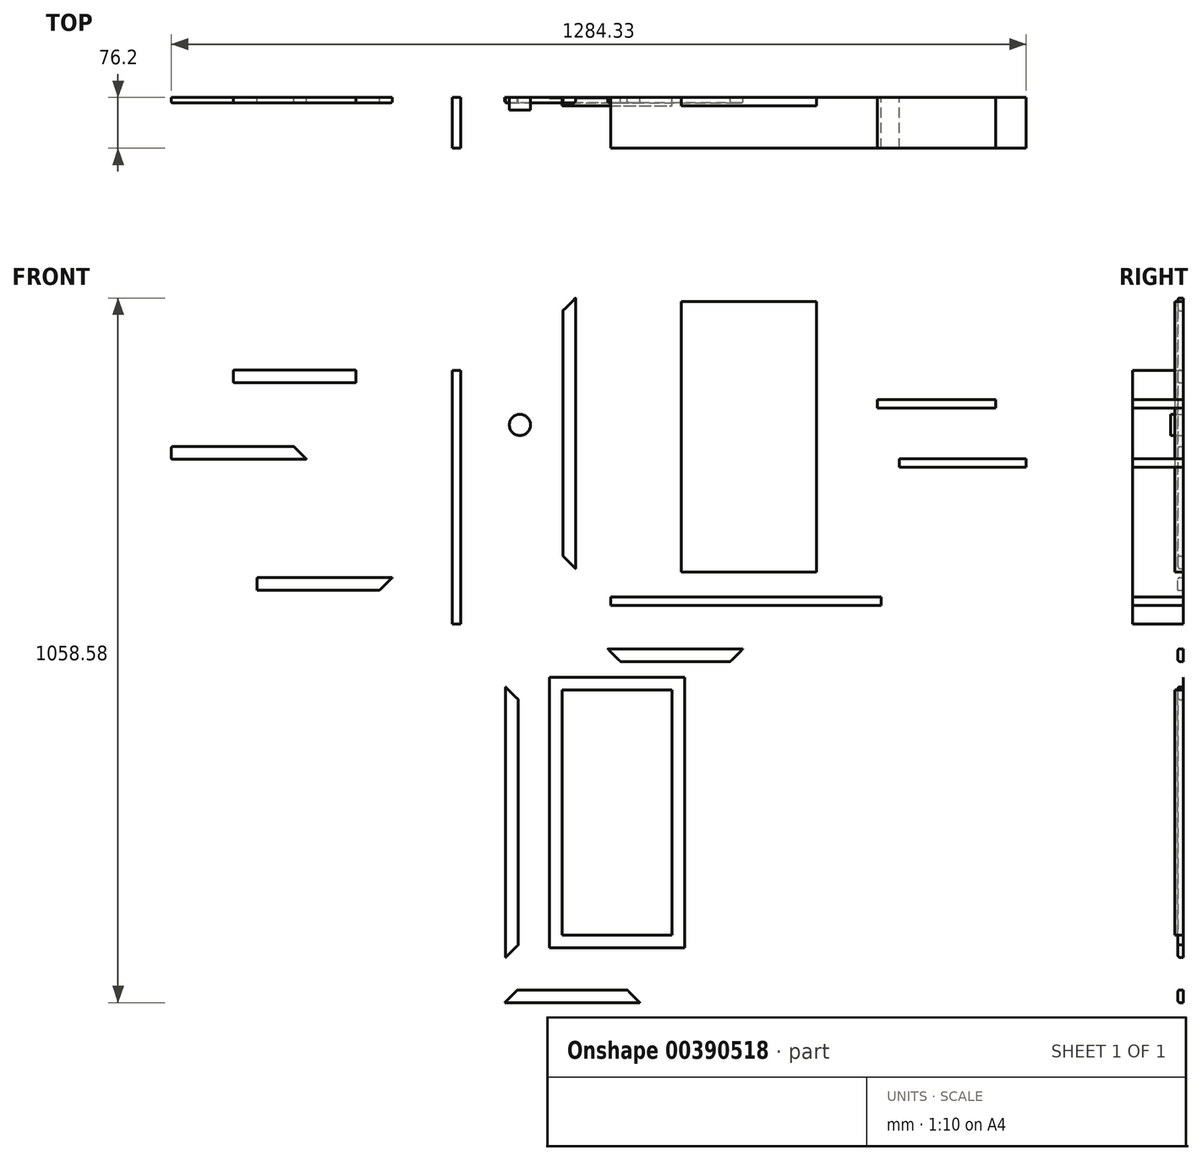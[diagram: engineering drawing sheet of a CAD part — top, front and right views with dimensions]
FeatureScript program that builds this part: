
annotation { "Feature Type Name" : "Feature", "Feature Type Description" : "" }
export const myFeature = defineFeature(function(context is Context, id is Id, definition is map)
    precondition{}
    {
        {
            var Q0;
            Q0=qCreatedBy(makeId("Front.planeOp"),FACE);
            var sketch = newSketch(context, id + "F0", { "sketchPlane" : qUnion([Q0])});
            skLineSegment(sketch, "E0.bottom", {"start": v(-101.6, 203.2) * mm, "end": v(101.6, 203.2) * mm});
            skLineSegment(sketch, "E0.top", {"start": v(-101.6, -203.2) * mm, "end": v(101.6, -203.2) * mm});
            skLineSegment(sketch, "E0.left", {"start": v(-101.6, 203.2) * mm, "end": v(-101.6, -203.2) * mm});
            skLineSegment(sketch, "E0.right", {"start": v(101.6, 203.2) * mm, "end": v(101.6, -203.2) * mm});
            skPoint(sketch, "E0.middle", {"position": v(0, 0) * mm});
            skSolve(sketch);
        }
        {
            var Q0;
            Q0 = qSketchRegion(id + "F0", true);
            extrude(context, id + "F1", {"entities" : qUnion([Q0]), "depth" : 12.7 * mm});
        }
        {
            var Q0;
            Q0=qCreatedBy(makeId("Front.planeOp"),FACE);
            var sketch = newSketch(context, id + "F2", { "sketchPlane" : qUnion([Q0])});
            skLineSegment(sketch, "E1.bottom", {"start": v(-445.4, 99.47) * mm, "end": v(-432.7, 99.47) * mm});
            skLineSegment(sketch, "E1.top", {"start": v(-445.4, -281.53) * mm, "end": v(-432.7, -281.53) * mm});
            skLineSegment(sketch, "E1.left", {"start": v(-445.4, 99.47) * mm, "end": v(-445.4, -281.53) * mm});
            skLineSegment(sketch, "E1.right", {"start": v(-432.7, 99.47) * mm, "end": v(-432.7, -281.53) * mm});
            skSolve(sketch);
        }
        {
            var Q0;
            Q0 = qSketchRegion(id + "F2", true);
            extrude(context, id + "F3", {"entities" : qUnion([Q0]), "depth" : 76.2 * mm});
        }
        {
            var Q0;
            Q0=qCreatedBy(makeId("Front.planeOp"),FACE);
            var sketch = newSketch(context, id + "F4", { "sketchPlane" : qUnion([Q0])});
            skLineSegment(sketch, "E2.bottom", {"start": v(-207.27, -253.72) * mm, "end": v(199.13, -253.72) * mm});
            skLineSegment(sketch, "E2.top", {"start": v(-207.27, -241.02) * mm, "end": v(199.13, -241.02) * mm});
            skLineSegment(sketch, "E2.left", {"start": v(-207.27, -253.72) * mm, "end": v(-207.27, -241.02) * mm});
            skLineSegment(sketch, "E2.right", {"start": v(199.13, -253.72) * mm, "end": v(199.13, -241.02) * mm});
            skSolve(sketch);
        }
        {
            var Q0;
            Q0 = qSketchRegion(id + "F4", true);
            extrude(context, id + "F5", {"entities" : qUnion([Q0]), "depth" : 76.2 * mm});
        }
        {
            var Q0;
            Q0=qCreatedBy(makeId("Front.planeOp"),FACE);
            var sketch = newSketch(context, id + "F6", { "sketchPlane" : qUnion([Q0])});
            skLineSegment(sketch, "E3.bottom", {"start": v(193.07, 55.39) * mm, "end": v(370.87, 55.39) * mm});
            skLineSegment(sketch, "E3.top", {"start": v(193.07, 42.69) * mm, "end": v(370.87, 42.69) * mm});
            skLineSegment(sketch, "E3.left", {"start": v(193.07, 55.39) * mm, "end": v(193.07, 42.69) * mm});
            skLineSegment(sketch, "E3.right", {"start": v(370.87, 55.39) * mm, "end": v(370.87, 42.69) * mm});
            skSolve(sketch);
        }
        {
            var Q0;
            Q0 = qSketchRegion(id + "F6", true);
            extrude(context, id + "F7", {"entities" : qUnion([Q0]), "depth" : 76.2 * mm});
        }
        {
            var Q0;
            Q0=qCreatedBy(makeId("Front.planeOp"),FACE);
            var sketch = newSketch(context, id + "F8", { "sketchPlane" : qUnion([Q0])});
            skLineSegment(sketch, "E4.bottom", {"start": v(226.2, -33.02) * mm, "end": v(416.7, -33.02) * mm});
            skLineSegment(sketch, "E4.top", {"start": v(226.2, -45.72) * mm, "end": v(416.7, -45.72) * mm});
            skLineSegment(sketch, "E4.left", {"start": v(226.2, -33.02) * mm, "end": v(226.2, -45.72) * mm});
            skLineSegment(sketch, "E4.right", {"start": v(416.7, -33.02) * mm, "end": v(416.7, -45.72) * mm});
            skSolve(sketch);
        }
        {
            var Q0;
            Q0 = qSketchRegion(id + "F8", true);
            extrude(context, id + "F9", {"entities" : qUnion([Q0]), "depth" : 76.2 * mm});
        }
        {
            var Q0;
            Q0=qCreatedBy(makeId("Front.planeOp"),FACE);
            var sketch = newSketch(context, id + "F10", { "sketchPlane" : qUnion([Q0])});
            skCircle(sketch, "E5", {"center": v(-343.97, 17.55) * mm, "radius": 15.88 * mm});
            skSolve(sketch);
        }
        {
            var Q0;
            Q0 = qSketchRegion(id + "F10", true);
            extrude(context, id + "F11", {"entities" : qUnion([Q0]), "depth" : 19.05 * mm});
        }
        {
            var Q0;
            Q0=qCreatedBy(makeId("Front.planeOp"),FACE);
            var sketch = newSketch(context, id + "F12", { "sketchPlane" : qUnion([Q0])});
            skLineSegment(sketch, "E6", {"start": v(-260.52, 208.27) * mm, "end": v(-279.57, 189.22) * mm});
            skLineSegment(sketch, "E7", {"start": v(-279.57, 189.22) * mm, "end": v(-279.57, -179.08) * mm});
            skLineSegment(sketch, "E8", {"start": v(-279.57, -179.08) * mm, "end": v(-260.52, -198.13) * mm});
            skLineSegment(sketch, "E9", {"start": v(-260.52, -198.13) * mm, "end": v(-260.52, 208.27) * mm});
            skSolve(sketch);
        }
        {
            var Q0;
            Q0 = qSketchRegion(id + "F12", true);
            extrude(context, id + "F13", {"entities" : qUnion([Q0]), "depth" : 7.94 * mm});
        }
        {
            var Q0;
            Q0=makeQuery(id+"F13.opExtrude","CAP_EDGE",EDGE,{"disambiguationData":[OSD([sQuery(id+"F12.wireOp",EDGE,"E9")])],"isStart":false});
            var Q1;
            Q1=makeQuery(id+"F13.opExtrude","CAP_EDGE",EDGE,{"disambiguationData":[OSD([sQuery(id+"F12.wireOp",EDGE,"E7")])],"isStart":false});
            fillet(context, id + "F14", {"entities" : qUnion([Q0, Q1]), "radius" : 2.54 * mm, "tangentPropagation" : true, "allowEdgeOverflow" : false});
        }
        {
            var Q0;
            Q0=qCreatedBy(makeId("Front.planeOp"),FACE);
            var sketch = newSketch(context, id + "F15", { "sketchPlane" : qUnion([Q0])});
            skLineSegment(sketch, "E10", {"start": v(-738.97, -211.91) * mm, "end": v(-738.97, -230.96) * mm});
            skLineSegment(sketch, "E11", {"start": v(-738.97, -230.96) * mm, "end": v(-554.82, -230.96) * mm});
            skLineSegment(sketch, "E12", {"start": v(-554.82, -230.96) * mm, "end": v(-535.77, -211.91) * mm});
            skLineSegment(sketch, "E13", {"start": v(-535.77, -211.91) * mm, "end": v(-738.97, -211.91) * mm});
            skSolve(sketch);
        }
        {
            var Q0;
            Q0 = qSketchRegion(id + "F15", true);
            extrude(context, id + "F16", {"entities" : qUnion([Q0]), "depth" : 7.94 * mm});
        }
        {
            var Q0;
            Q0=makeQuery(id+"F16.opExtrude","CAP_EDGE",EDGE,{"disambiguationData":[OSD([sQuery(id+"F15.wireOp",EDGE,"E13")])],"isStart":false});
            fillet(context, id + "F17", {"entities" : qUnion([Q0]), "radius" : 2.54 * mm, "tangentPropagation" : true, "allowEdgeOverflow" : false});
        }
        {
            var Q0;
            Q0=makeQuery(id+"F16.opExtrude","CAP_EDGE",EDGE,{"disambiguationData":[OSD([sQuery(id+"F15.wireOp",EDGE,"E10")])],"isStart":false});
            fillet(context, id + "F18", {"entities" : qUnion([Q0]), "radius" : 1.27 * mm, "tangentPropagation" : true, "allowEdgeOverflow" : false});
        }
        {
            var Q0;
            Q0=qCreatedBy(makeId("Front.planeOp"),FACE);
            var sketch = newSketch(context, id + "F19", { "sketchPlane" : qUnion([Q0])});
            skLineSegment(sketch, "E14", {"start": v(-867.62, -15.18) * mm, "end": v(-867.62, -34.23) * mm});
            skLineSegment(sketch, "E15", {"start": v(-867.62, -34.23) * mm, "end": v(-664.42, -34.23) * mm});
            skLineSegment(sketch, "E16", {"start": v(-664.42, -34.23) * mm, "end": v(-683.47, -15.18) * mm});
            skLineSegment(sketch, "E17", {"start": v(-683.47, -15.18) * mm, "end": v(-867.62, -15.18) * mm});
            skSolve(sketch);
        }
        {
            var Q0;
            Q0=makeQuery(id+"F19.imprint","IMPRINT",FACE,{"disambiguationData":[TD([[makeQuery(id+"F19.imprint","IMPRINT",EDGE,{"derivedFrom":sQuery(id+"F19.wireOp",EDGE,"E14")}),1.0]])]});
            extrude(context, id + "F20", {"entities" : qUnion([Q0]), "depth" : 7.94 * mm});
        }
        {
            var Q0;
            Q0=makeQuery(id+"F20.opExtrude","CAP_EDGE",EDGE,{"disambiguationData":[OSD([sQuery(id+"F19.wireOp",EDGE,"E15")])],"isStart":false});
            var Q1;
            Q1=makeQuery(id+"F20.opExtrude","CAP_EDGE",EDGE,{"disambiguationData":[OSD([sQuery(id+"F19.wireOp",EDGE,"E17")])],"isStart":false});
            fillet(context, id + "F21", {"entities" : qUnion([Q0, Q1]), "radius" : 2.54 * mm, "tangentPropagation" : true, "allowEdgeOverflow" : false});
        }
        {
            var Q0;
            Q0=makeQuery(id+"F20.opExtrude","CAP_EDGE",EDGE,{"disambiguationData":[OSD([sQuery(id+"F19.wireOp",EDGE,"E14")])],"isStart":false});
            fillet(context, id + "F22", {"entities" : qUnion([Q0]), "radius" : 1.27 * mm, "tangentPropagation" : true, "allowEdgeOverflow" : false});
        }
        {
            var Q0;
            Q0=qCreatedBy(makeId("Front.planeOp"),FACE);
            var sketch = newSketch(context, id + "F23", { "sketchPlane" : qUnion([Q0])});
            skLineSegment(sketch, "E18.bottom", {"start": v(-774.39, 99.94) * mm, "end": v(-590.24, 99.94) * mm});
            skLineSegment(sketch, "E18.top", {"start": v(-774.39, 80.9) * mm, "end": v(-590.24, 80.9) * mm});
            skLineSegment(sketch, "E18.left", {"start": v(-774.39, 99.94) * mm, "end": v(-774.39, 80.9) * mm});
            skLineSegment(sketch, "E18.right", {"start": v(-590.24, 99.94) * mm, "end": v(-590.24, 80.9) * mm});
            skSolve(sketch);
        }
        {
            var Q0;
            Q0=makeQuery(id+"F23.imprint","IMPRINT",FACE,{"disambiguationData":[TD([[makeQuery(id+"F23.imprint","IMPRINT",EDGE,{"derivedFrom":sQuery(id+"F23.wireOp",EDGE,"E18.bottom")}),-1.0]])]});
            extrude(context, id + "F24", {"entities" : qUnion([Q0]), "depth" : 7.94 * mm});
        }
        {
            var Q0;
            Q0=makeQuery(id+"F24.opExtrude","CAP_EDGE",EDGE,{"disambiguationData":[OSD([sQuery(id+"F23.wireOp",EDGE,"E18.bottom")])],"isStart":false});
            var Q1;
            Q1=makeQuery(id+"F24.opExtrude","CAP_EDGE",EDGE,{"disambiguationData":[OSD([sQuery(id+"F23.wireOp",EDGE,"E18.top")])],"isStart":false});
            fillet(context, id + "F25", {"entities" : qUnion([Q0, Q1]), "radius" : 2.54 * mm, "tangentPropagation" : true, "allowEdgeOverflow" : false});
        }
        {
            var Q0;
            Q0=makeQuery(id+"F24.opExtrude","CAP_EDGE",EDGE,{"disambiguationData":[OSD([sQuery(id+"F23.wireOp",EDGE,"E18.left")])],"isStart":false});
            var Q1;
            Q1=makeQuery(id+"F24.opExtrude","CAP_EDGE",EDGE,{"disambiguationData":[OSD([sQuery(id+"F23.wireOp",EDGE,"E18.right")])],"isStart":false});
            fillet(context, id + "F26", {"entities" : qUnion([Q0, Q1]), "radius" : 1.27 * mm, "tangentPropagation" : true, "allowEdgeOverflow" : false});
        }
        {
            var Q0;
            Q0=qCreatedBy(makeId("Front.planeOp"),FACE);
            var sketch = newSketch(context, id + "F27", { "sketchPlane" : qUnion([Q0])});
            skLineSegment(sketch, "E19.bottom", {"start": v(-299.3, -361.37) * mm, "end": v(-96.1, -361.37) * mm});
            skLineSegment(sketch, "E19.top", {"start": v(-299.3, -767.77) * mm, "end": v(-96.1, -767.77) * mm});
            skLineSegment(sketch, "E19.left", {"start": v(-299.3, -361.37) * mm, "end": v(-299.3, -767.77) * mm});
            skLineSegment(sketch, "E19.right", {"start": v(-96.1, -361.37) * mm, "end": v(-96.1, -767.77) * mm});
            skPoint(sketch, "E19.middle", {"position": v(-197.7, -564.57) * mm});
            skSolve(sketch);
        }
        {
            var Q0;
            Q0=qCreatedBy(makeId("Front.planeOp"),FACE);
            var sketch = newSketch(context, id + "F28", { "sketchPlane" : qUnion([Q0])});
            skLineSegment(sketch, "E20.bottom", {"start": v(-280.26, -380.42) * mm, "end": v(-115.16, -380.42) * mm});
            skLineSegment(sketch, "E20.top", {"start": v(-280.26, -748.72) * mm, "end": v(-115.16, -748.72) * mm});
            skLineSegment(sketch, "E20.left", {"start": v(-280.26, -380.42) * mm, "end": v(-280.26, -748.72) * mm});
            skLineSegment(sketch, "E20.right", {"start": v(-115.16, -380.42) * mm, "end": v(-115.16, -748.72) * mm});
            skSolve(sketch);
        }
        {
            var Q0;
            Q0 = qSketchRegion(id + "F27", true);
            extrude(context, id + "F29", {"entities" : qUnion([Q0]), "depth" : (.5 - (5 / 16)) * mm});
        }
        {
            var Q0;
            Q0 = qSketchRegion(id + "F28", true);
            extrude(context, id + "F30", {"entities" : qUnion([Q0]), "operationType" : NewBodyOperationType.ADD, "depth" : 12.7 * mm});
        }
        {
            var Q0;
            Q0=qCreatedBy(makeId("Front.planeOp"),FACE);
            var sketch = newSketch(context, id + "F31", { "sketchPlane" : qUnion([Q0])});
            skLineSegment(sketch, "E21", {"start": v(-211.89, -318.78) * mm, "end": v(-192.84, -337.83) * mm});
            skLineSegment(sketch, "E22", {"start": v(-192.84, -337.83) * mm, "end": v(-27.74, -337.83) * mm});
            skLineSegment(sketch, "E23", {"start": v(-27.74, -337.83) * mm, "end": v(-8.69, -318.78) * mm});
            skLineSegment(sketch, "E24", {"start": v(-8.69, -318.78) * mm, "end": v(-211.89, -318.78) * mm});
            skSolve(sketch);
        }
        {
            var Q0;
            Q0 = qSketchRegion(id + "F31", true);
            extrude(context, id + "F32", {"entities" : qUnion([Q0]), "depth" : 7.94 * mm});
        }
        {
            var Q0;
            Q0=makeQuery(id+"F32.opExtrude","CAP_EDGE",EDGE,{"disambiguationData":[OSD([sQuery(id+"F31.wireOp",EDGE,"E22")])],"isStart":false});
            var Q1;
            Q1=makeQuery(id+"F32.opExtrude","CAP_EDGE",EDGE,{"disambiguationData":[OSD([sQuery(id+"F31.wireOp",EDGE,"E24")])],"isStart":false});
            fillet(context, id + "F33", {"entities" : qUnion([Q0, Q1]), "radius" : 2.54 * mm, "tangentPropagation" : true, "allowEdgeOverflow" : false});
        }
        {
            var Q0;
            Q0=qCreatedBy(makeId("Front.planeOp"),FACE);
            var sketch = newSketch(context, id + "F34", { "sketchPlane" : qUnion([Q0])});
            skLineSegment(sketch, "E25", {"start": v(-347.6, -831.26) * mm, "end": v(-366.66, -850.31) * mm});
            skLineSegment(sketch, "E26", {"start": v(-366.66, -850.31) * mm, "end": v(-163.46, -850.31) * mm});
            skLineSegment(sketch, "E27", {"start": v(-163.46, -850.31) * mm, "end": v(-182.5, -831.26) * mm});
            skLineSegment(sketch, "E28", {"start": v(-182.5, -831.26) * mm, "end": v(-347.6, -831.26) * mm});
            skSolve(sketch);
        }
        {
            var Q0;
            Q0=makeQuery(id+"F34.imprint","IMPRINT",FACE,{"disambiguationData":[TD([[makeQuery(id+"F34.imprint","IMPRINT",EDGE,{"derivedFrom":sQuery(id+"F34.wireOp",EDGE,"E25")}),1.0]])]});
            extrude(context, id + "F35", {"entities" : qUnion([Q0]), "depth" : 7.94 * mm});
        }
        {
            var Q0;
            Q0=makeQuery(id+"F35.opExtrude","CAP_EDGE",EDGE,{"disambiguationData":[OSD([sQuery(id+"F34.wireOp",EDGE,"E26")])],"isStart":false});
            var Q1;
            Q1=makeQuery(id+"F35.opExtrude","CAP_EDGE",EDGE,{"disambiguationData":[OSD([sQuery(id+"F34.wireOp",EDGE,"E28")])],"isStart":false});
            fillet(context, id + "F36", {"entities" : qUnion([Q0, Q1]), "radius" : 2.54 * mm, "tangentPropagation" : true, "allowEdgeOverflow" : false});
        }
        {
            var Q0;
            Q0=qCreatedBy(makeId("Front.planeOp"),FACE);
            var sketch = newSketch(context, id + "F37", { "sketchPlane" : qUnion([Q0])});
            skLineSegment(sketch, "E29", {"start": v(-346.25, -395.02) * mm, "end": v(-365.3, -375.97) * mm});
            skLineSegment(sketch, "E30", {"start": v(-365.3, -375.97) * mm, "end": v(-365.3, -782.37) * mm});
            skLineSegment(sketch, "E31", {"start": v(-365.3, -782.37) * mm, "end": v(-346.25, -763.32) * mm});
            skLineSegment(sketch, "E32", {"start": v(-346.25, -763.32) * mm, "end": v(-346.25, -395.02) * mm});
            skSolve(sketch);
        }
        {
            var Q0;
            Q0=makeQuery(id+"F37.imprint","IMPRINT",FACE,{"disambiguationData":[TD([[makeQuery(id+"F37.imprint","IMPRINT",EDGE,{"derivedFrom":sQuery(id+"F37.wireOp",EDGE,"E29")}),1.0]])]});
            extrude(context, id + "F38", {"entities" : qUnion([Q0]), "depth" : 7.94 * mm});
        }
        {
            var Q0;
            Q0=makeQuery(id+"F38.opExtrude","CAP_EDGE",EDGE,{"disambiguationData":[OSD([sQuery(id+"F37.wireOp",EDGE,"E30")])],"isStart":false});
            var Q1;
            Q1=makeQuery(id+"F38.opExtrude","CAP_EDGE",EDGE,{"disambiguationData":[OSD([sQuery(id+"F37.wireOp",EDGE,"E32")])],"isStart":false});
            fillet(context, id + "F39", {"entities" : qUnion([Q0, Q1]), "radius" : 2.54 * mm, "tangentPropagation" : true, "allowEdgeOverflow" : false});
        }
    });
